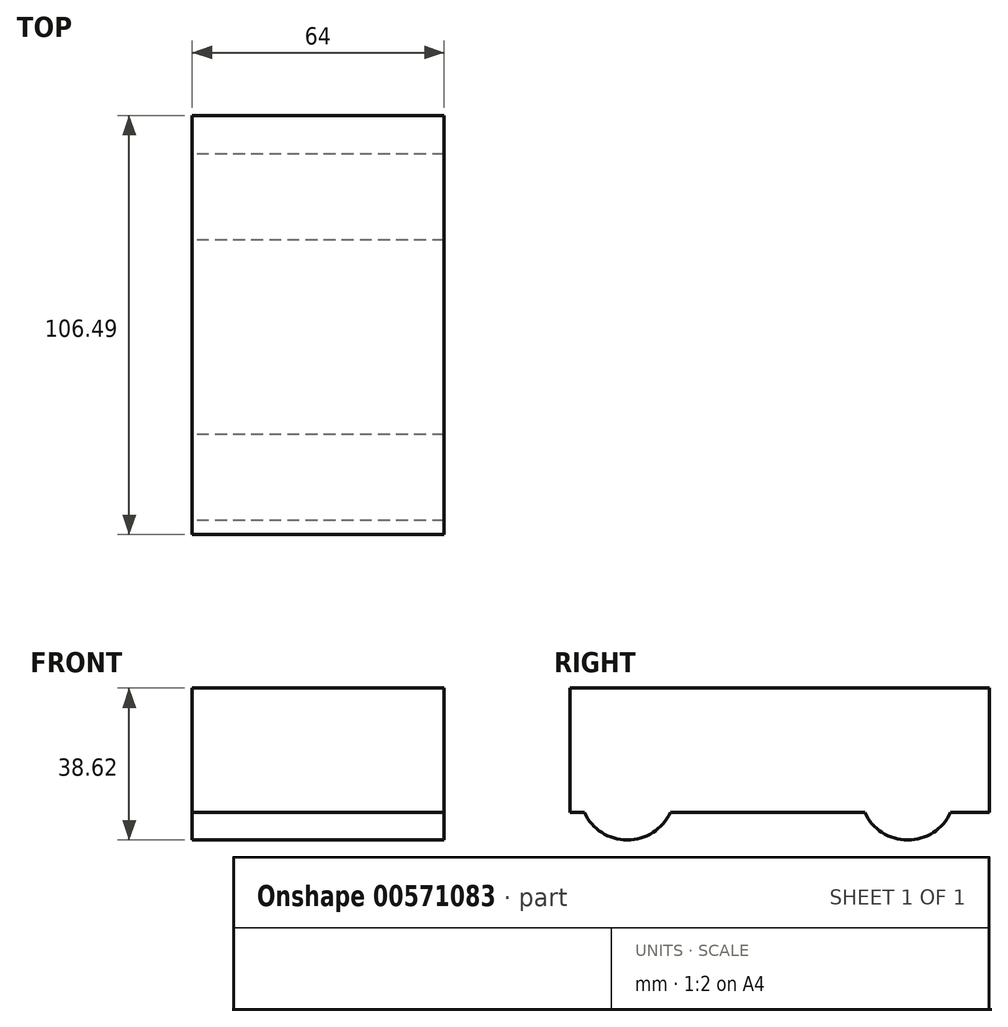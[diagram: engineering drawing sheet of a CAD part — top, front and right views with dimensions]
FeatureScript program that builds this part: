
annotation { "Feature Type Name" : "Feature", "Feature Type Description" : "" }
export const myFeature = defineFeature(function(context is Context, id is Id, definition is map)
    precondition{}
    {
        {
            var Q0;
            Q0=qCreatedBy(makeId("Right.planeOp"),FACE);
            var sketch = newSketch(context, id + "F0", { "sketchPlane" : qUnion([Q0])});
            skLineSegment(sketch, "E0", {"start": v(-37.34, -5) * mm, "end": v(-37.34, 26.62) * mm});
            skLineSegment(sketch, "E1", {"start": v(-37.34, 26.62) * mm, "end": v(69.15, 26.62) * mm});
            skLineSegment(sketch, "E2", {"start": v(69.15, 26.62) * mm, "end": v(69.15, -5) * mm});
            skLineSegment(sketch, "E3", {"start": v(69.15, -5) * mm, "end": v(-37.34, -5) * mm});
            skCircle(sketch, "E4", {"center": v(-22.8, 0) * mm, "radius": 12 * mm});
            skCircle(sketch, "E5", {"center": v(48.43, 0) * mm, "radius": 12 * mm});
            skLineSegment(sketch, "E6", {"start": v(36.43, 0) * mm, "end": v(36.43, -5) * mm});
            skLineSegment(sketch, "E7", {"start": v(60.43, 0) * mm, "end": v(60.43, -5) * mm});
            skSolve(sketch);
        }
        {
            var Q0;
            {var subQ5=sQuery(id+"F0.wireOp",EDGE,"E0");Q0=makeQuery(id+"F0.imprint","IMPRINT",FACE,{"disambiguationData":[TD([[makeQuery(id+"F0.imprint","IMPRINT",EDGE,{"derivedFrom":subQ5}),-1.0]])]});}
            var Q1;
            {var subQ0=sQuery(id+"F0.wireOp",EDGE,"E6");Q1=makeQuery(id+"F0.imprint","IMPRINT",FACE,{"disambiguationData":[TD([[makeQuery(id+"F0.imprint","IMPRINT",EDGE,{"derivedFrom":subQ0}),1.0]])]});}
            var Q2;
            {var subQ0=sQuery(id+"F0.wireOp",EDGE,"E4");var subQ1=sQuery(id+"F0.wireOp",EDGE,"E3");var subQ2=makeQuery(id+"F0.imprint","INTERSECT",VERTEX,{"disambiguationData":[OD(0.0)],"derivedFrom":[subQ1,subQ0]});Q2=makeQuery(id+"F0.imprint","IMPRINT",FACE,{"disambiguationData":[TD([[makeQuery(id+"F0.imprint","IMPRINT",EDGE,{"disambiguationData":[TD([[subQ2,-1.0]])],"derivedFrom":subQ1}),-1.0]])]});}
            var Q3;
            {var subQ0=sQuery(id+"F0.wireOp",EDGE,"E5");var subQ1=sQuery(id+"F0.wireOp",EDGE,"E3");var subQ2=makeQuery(id+"F0.imprint","INTERSECT",VERTEX,{"disambiguationData":[OD(0.0)],"derivedFrom":[subQ1,subQ0]});Q3=makeQuery(id+"F0.imprint","IMPRINT",FACE,{"disambiguationData":[TD([[makeQuery(id+"F0.imprint","IMPRINT",EDGE,{"disambiguationData":[TD([[subQ2,-1.0]])],"derivedFrom":subQ1}),-1.0]])]});}
            var Q4;
            {var subQ0=sQuery(id+"F0.wireOp",EDGE,"E7");Q4=makeQuery(id+"F0.imprint","IMPRINT",FACE,{"disambiguationData":[TD([[makeQuery(id+"F0.imprint","IMPRINT",EDGE,{"derivedFrom":subQ0}),-1.0]])]});}
            var Q5;
            {var subQ0=sQuery(id+"F0.wireOp",EDGE,"E4");var subQ1=sQuery(id+"F0.wireOp",EDGE,"E3");var subQ2=makeQuery(id+"F0.imprint","INTERSECT",VERTEX,{"disambiguationData":[OD(0.0)],"derivedFrom":[subQ1,subQ0]});Q5=makeQuery(id+"F0.imprint","IMPRINT",FACE,{"disambiguationData":[TD([[makeQuery(id+"F0.imprint","IMPRINT",EDGE,{"disambiguationData":[TD([[subQ2,-1.0]])],"derivedFrom":subQ1}),1.0]])]});}
            var Q6;
            {var subQ0=sQuery(id+"F0.wireOp",EDGE,"E5");var subQ1=sQuery(id+"F0.wireOp",EDGE,"E3");var subQ2=makeQuery(id+"F0.imprint","INTERSECT",VERTEX,{"disambiguationData":[OD(0.0)],"derivedFrom":[subQ1,subQ0]});Q6=makeQuery(id+"F0.imprint","IMPRINT",FACE,{"disambiguationData":[TD([[makeQuery(id+"F0.imprint","IMPRINT",EDGE,{"disambiguationData":[TD([[subQ2,-1.0]])],"derivedFrom":subQ1}),1.0]])]});}
            extrude(context, id + "F1", {"entities" : qUnion([Q0, Q1, Q2, Q3, Q4, Q5, Q6]), "endBound" : BoundingType.SYMMETRIC, "depth" : 64 * mm, "offsetDistance" : 25 * mm});
        }
    });
